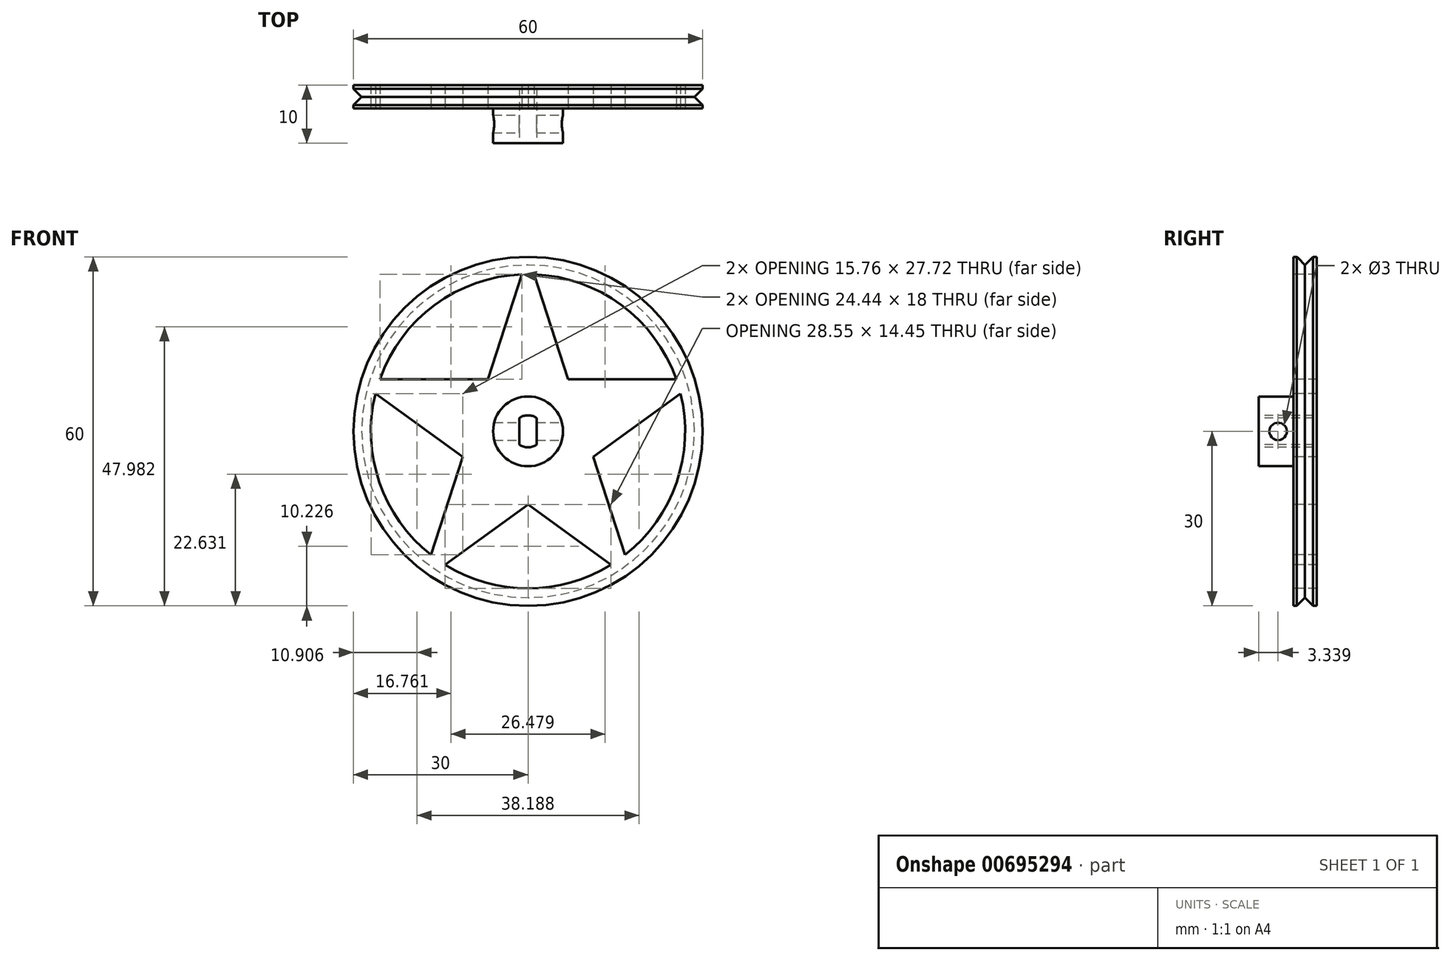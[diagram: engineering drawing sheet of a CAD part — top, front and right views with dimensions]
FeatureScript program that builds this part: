
annotation { "Feature Type Name" : "Feature", "Feature Type Description" : "" }
export const myFeature = defineFeature(function(context is Context, id is Id, definition is map)
    precondition{}
    {
        {
            var Q0;
            Q0=qCreatedBy(makeId("Front.planeOp"),FACE);
            var sketch = newSketch(context, id + "F0", { "sketchPlane" : qUnion([Q0])});
            skCircle(sketch, "E0", {"center": v(0, 0) * mm, "radius": 30 * mm});
            skCircle(sketch, "E1", {"center": v(0, 0) * mm, "radius": 6 * mm});
            skSolve(sketch);
        }
        {
            var Q0;
            Q0=makeQuery(id+"F0.imprint","IMPRINT",FACE,{"disambiguationData":[TD([[makeQuery(id+"F0.imprint","IMPRINT",EDGE,{"derivedFrom":sQuery(id+"F0.wireOp",EDGE,"E1")}),1.0]])]});
            extrude(context, id + "F1", {"entities" : qUnion([Q0]), "depth" : 10 * mm, "offsetDistance" : 25 * mm});
        }
        {
            var Q0;
            Q0 = qSketchRegion(id + "F0", true);
            extrude(context, id + "F2", {"entities" : qUnion([Q0]), "operationType" : NewBodyOperationType.ADD, "depth" : 4 * mm, "offsetDistance" : 25 * mm});
        }
        {
            var Q0;
            Q0=qCreatedBy(makeId("Right.planeOp"),FACE);
            var sketch = newSketch(context, id + "F3", { "sketchPlane" : qUnion([Q0])});
            skCircle(sketch, "E2", {"center": v(-6.66, 0) * mm, "radius": 1.5 * mm});
            skSolve(sketch);
        }
        {
            var Q0;
            Q0 = qSketchRegion(id + "F3", true);
            extrude(context, id + "F4", {"entities" : qUnion([Q0]), "operationType" : NewBodyOperationType.REMOVE, "oppositeDirection" : true, "depth" : 25.3 * mm, "offsetDistance" : 25 * mm, "hasSecondDirection" : true, "secondDirectionOppositeDirection" : false, "secondDirectionDepth" : 25 * mm});
        }
        {
            var Q0;
            Q0=makeQuery(id+"F1.opExtrude","CAP_FACE",FACE,{"disambiguationData":[OSD([sQuery(id+"F0.wireOp",EDGE,"E1")])],"isStart":false});
            var sketch = newSketch(context, id + "F5", { "sketchPlane" : qUnion([Q0])});
            skLineSegment(sketch, "E3.left", {"start": v(1.5, -2.3) * mm, "end": v(1.5, 2.3) * mm});
            skLineSegment(sketch, "E3.right", {"start": v(-1.5, -2.3) * mm, "end": v(-1.5, 2.3) * mm});
            skPoint(sketch, "E3.middle", {"position": v(0, 0) * mm});
            skArc(sketch, "E4", {"start": v(1.5, 2.3) * mm, "mid": v(0, 2.75) * mm, "end": v(-1.5, 2.3) * mm});
            skArc(sketch, "E5", {"start": v(-1.5, -2.3) * mm, "mid": v(0, -2.75) * mm, "end": v(1.5, -2.3) * mm});
            skSolve(sketch);
        }
        {
            var Q0;
            Q0 = qSketchRegion(id + "F5", true);
            extrude(context, id + "F6", {"entities" : qUnion([Q0]), "operationType" : NewBodyOperationType.REMOVE, "oppositeDirection" : true, "depth" : 9.4 * mm, "offsetDistance" : 25 * mm});
        }
        {
            var Q0;
            Q0=qCreatedBy(makeId("Right.planeOp"),FACE);
            var sketch = newSketch(context, id + "F7", { "sketchPlane" : qUnion([Q0])});
            skLineSegment(sketch, "E6", {"start": v(-0.63, -30) * mm, "end": v(-3.46, -30) * mm});
            skLineSegment(sketch, "E7", {"start": v(0, -30) * mm, "end": v(-4, -30) * mm, "construction": true});
            skLineSegment(sketch, "E8", {"start": v(0, -30) * mm, "end": v(-4, -30) * mm});
            skLineSegment(sketch, "E9", {"start": v(-0.24, -30) * mm, "end": v(-4, -30) * mm, "construction": true});
            skLineSegment(sketch, "E10", {"start": v(-3.46, -30) * mm, "end": v(-2.04, -28.59) * mm});
            skLineSegment(sketch, "E11", {"start": v(-2.04, -28.59) * mm, "end": v(-0.63, -30) * mm});
            skLineSegment(sketch, "E12", {"start": v(-2.12, -30) * mm, "end": v(-2.04, -26.61) * mm, "construction": true});
            skLineSegment(sketch, "E13", {"start": v(-16.46, 0) * mm, "end": v(8.19, 0) * mm, "construction": true});
            skSolve(sketch);
        }
        {
            var Q0;
            Q0 = qSketchRegion(id + "F7", true);
            var Q1;
            Q1=sQuery(id+"F7.wireOp",EDGE,"E13");
            revolve(context, id + "F8", {"operationType" : NewBodyOperationType.REMOVE, "surfaceOperationType" : NewSurfaceOperationType.NEW, "entities" : qUnion([Q0]), "axis" : qUnion([Q1]), "revolveType" : RevolveType.FULL, "oppositeDirection" : true});
        }
        {
            var Q0;
            Q0=makeQuery(id+"F2.opExtrude","CAP_FACE",FACE,{"disambiguationData":[OSD([sQuery(id+"F0.wireOp",EDGE,"E0"),sQuery(id+"F0.wireOp",EDGE,"E1")])],"isStart":false});
            var sketch = newSketch(context, id + "F9", { "sketchPlane" : qUnion([Q0])});
            skCircle(sketch, "E14", {"center": v(0, 0) * mm, "radius": 27 * mm});
            skSolve(sketch);
        }
        {
            var Q0;
            Q0=makeQuery(id+"F9.imprint","IMPRINT",FACE,{"disambiguationData":[TD([[makeQuery(id+"F9.imprint","IMPRINT",EDGE,{"derivedFrom":sQuery(id+"F9.wireOp",EDGE,"E14")}),1.0]])]});
            var sketch = newSketch(context, id + "F10", { "sketchPlane" : qUnion([Q0])});
            skLineSegment(sketch, "E15", {"start": v(-18.14, -25.73) * mm, "end": v(-11.21, -4.4) * mm});
            skLineSegment(sketch, "E16", {"start": v(0, 30.11) * mm, "end": v(6.86, 8.98) * mm});
            skLineSegment(sketch, "E17", {"start": v(18.14, -25.73) * mm, "end": v(0, -12.55) * mm});
            skLineSegment(sketch, "E18", {"start": v(0, -12.55) * mm, "end": v(-18.14, -25.73) * mm});
            skLineSegment(sketch, "E19", {"start": v(-29.64, 8.98) * mm, "end": v(-6.86, 8.98) * mm});
            skLineSegment(sketch, "E20", {"start": v(29.64, 8.98) * mm, "end": v(11.21, -4.4) * mm});
            skLineSegment(sketch, "E21", {"start": v(-29.64, 8.98) * mm, "end": v(-11.21, -4.4) * mm});
            skLineSegment(sketch, "E22.trimOffspring", {"start": v(6.86, 8.98) * mm, "end": v(29.64, 8.98) * mm});
            skLineSegment(sketch, "E23.trimOffspring", {"start": v(-6.86, 8.98) * mm, "end": v(0, 30.11) * mm});
            skLineSegment(sketch, "E24.trimOffspring", {"start": v(11.21, -4.4) * mm, "end": v(18.14, -25.73) * mm});
            skSolve(sketch);
        }
        {
            var Q0;
            {var subQ0=sQuery(id+"F10.wireOp",EDGE,"E18");var subQ1=sQuery(id+"F10.wireOp",EDGE,"E17");var subQ2=makeQuery(id+"F10.imprint","INTERSECT",VERTEX,{"derivedFrom":[subQ1,subQ0]});Q0=makeQuery(id+"F10.imprint","IMPRINT",FACE,{"disambiguationData":[TD([[makeQuery(id+"F10.imprint","IMPRINT",EDGE,{"disambiguationData":[TD([[subQ2,1.0]])],"derivedFrom":subQ1}),1.0]])]});}
            var Q1;
            {var subQ0=sQuery(id+"F10.wireOp",EDGE,"E21");var subQ1=sQuery(id+"F10.wireOp",EDGE,"E15");var subQ2=makeQuery(id+"F10.imprint","INTERSECT",VERTEX,{"derivedFrom":[subQ1,subQ0]});Q1=makeQuery(id+"F10.imprint","IMPRINT",FACE,{"disambiguationData":[TD([[makeQuery(id+"F10.imprint","IMPRINT",EDGE,{"disambiguationData":[TD([[subQ2,1.0]])],"derivedFrom":subQ1}),1.0]])]});}
            var Q2;
            {var subQ0=sQuery(id+"F10.wireOp",EDGE,"E23.trimOffspring");var subQ1=sQuery(id+"F10.wireOp",EDGE,"E19");var subQ2=makeQuery(id+"F10.imprint","INTERSECT",VERTEX,{"derivedFrom":[subQ1,subQ0]});Q2=makeQuery(id+"F10.imprint","IMPRINT",FACE,{"disambiguationData":[TD([[makeQuery(id+"F10.imprint","IMPRINT",EDGE,{"disambiguationData":[TD([[subQ2,1.0]])],"derivedFrom":subQ1}),1.0]])]});}
            var Q3;
            {var subQ0=sQuery(id+"F10.wireOp",EDGE,"E22.trimOffspring");var subQ1=sQuery(id+"F10.wireOp",EDGE,"E16");var subQ2=makeQuery(id+"F10.imprint","INTERSECT",VERTEX,{"derivedFrom":[subQ1,subQ0]});Q3=makeQuery(id+"F10.imprint","IMPRINT",FACE,{"disambiguationData":[TD([[makeQuery(id+"F10.imprint","IMPRINT",EDGE,{"disambiguationData":[TD([[subQ2,1.0]])],"derivedFrom":subQ1}),1.0]])]});}
            var Q4;
            {var subQ0=sQuery(id+"F10.wireOp",EDGE,"E24.trimOffspring");var subQ1=sQuery(id+"F10.wireOp",EDGE,"E20");var subQ2=makeQuery(id+"F10.imprint","INTERSECT",VERTEX,{"derivedFrom":[subQ1,subQ0]});Q4=makeQuery(id+"F10.imprint","IMPRINT",FACE,{"disambiguationData":[TD([[makeQuery(id+"F10.imprint","IMPRINT",EDGE,{"disambiguationData":[TD([[subQ2,1.0]])],"derivedFrom":subQ1}),1.0]])]});}
            extrude(context, id + "F11", {"entities" : qUnion([Q0, Q1, Q2, Q3, Q4]), "operationType" : NewBodyOperationType.REMOVE, "oppositeDirection" : true, "depth" : 25 * mm, "offsetDistance" : 25 * mm});
        }
    });
